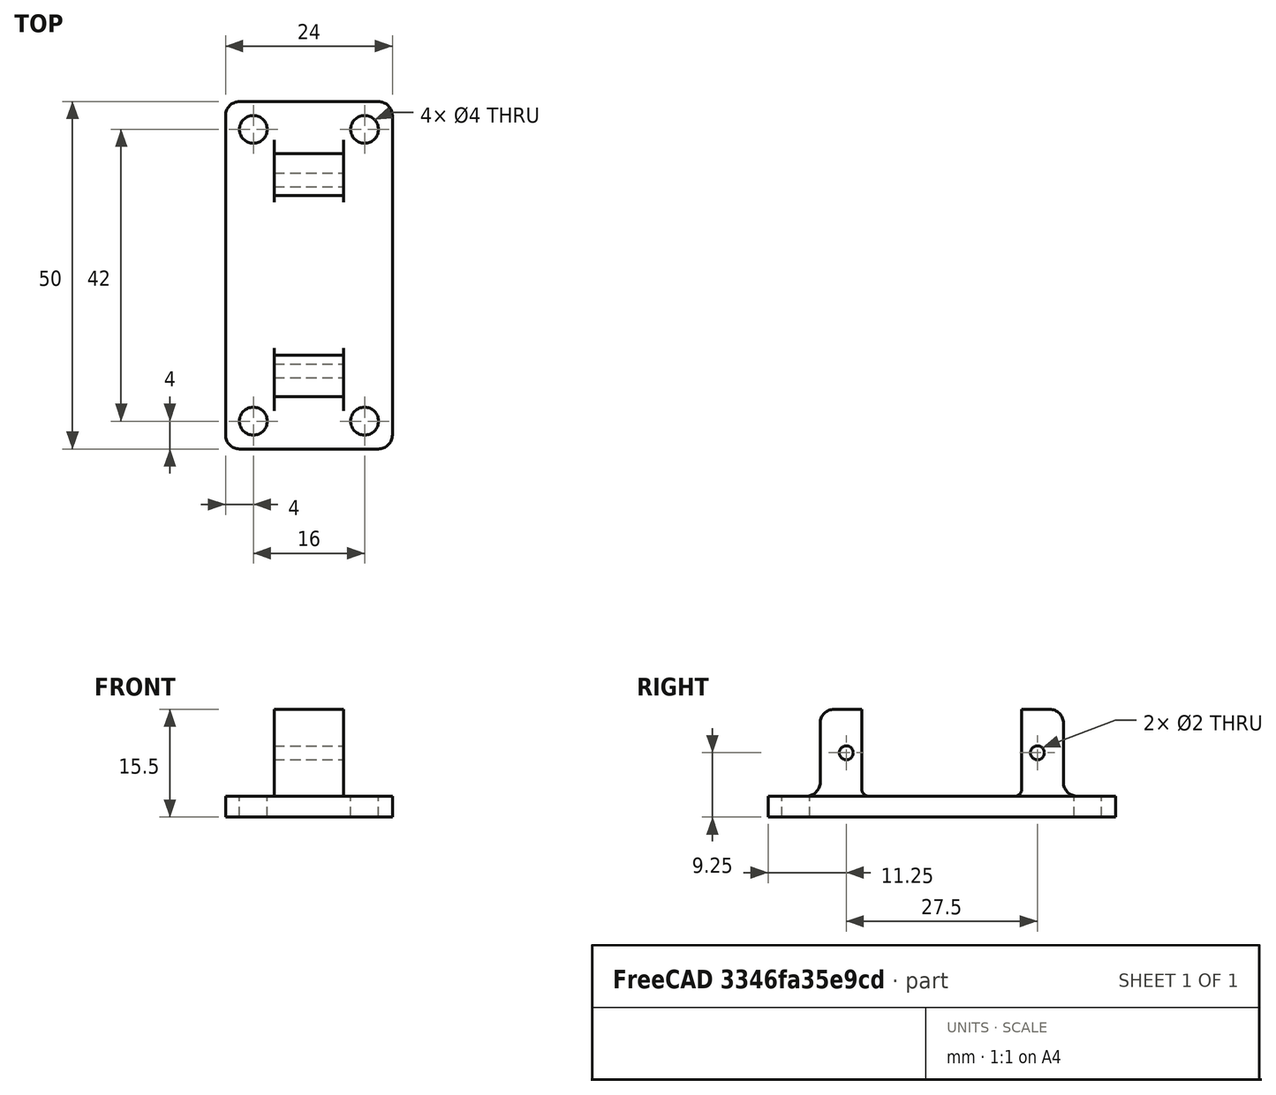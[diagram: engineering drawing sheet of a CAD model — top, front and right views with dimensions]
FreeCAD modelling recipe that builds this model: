
FCSTD DOCUMENT  (FreeCAD 0.19R24276 (Git))
Label: ServoBase
License: All rights reserved
LicenseURL: http://en.wikipedia.org/wiki/All_rights_reserved
objects: Part::Cylinder×6, Part::Fillet×4, Part::Box×3, Part::Cut×2, Part::MultiFuse×2, Spreadsheet::Sheet×1
note: 17 computed .brp shape members not serialized (recipe doc carries the construction recipe); baked Part::Feature solids carry a one-line shape summary decoded from their .brp

FEATURE [Part::Box] Box  label="base"
  AttacherType = Attacher::AttachEngine3D
  Height = 3
  Length = 24
  Width = 50
  expr: Length = <<data>>.base_depth
  expr: Width = <<data>>.base_width
FEATURE [Part::Box] Box001  label="Cube"
  AttacherType = Attacher::AttachEngine3D
  Height = 12.5
  Length = 10
  Placement = pos=(7,7.5,3) rot=(0,0,1;0rad)
  Width = 35
  expr: .Placement.Base.y = (<<data>>.base_width - 35mm) / 2
FEATURE [Part::Box] Box002  label="Cube001"
  AttacherType = Attacher::AttachEngine3D
  Height = 12.5
  Length = 16
  Placement = pos=(7,13.5,3) rot=(0,0,1;0rad)
  Width = 23
  expr: .Placement.Base.y = (<<data>>.base_width - 35mm) / 2 + 6mm
FEATURE [Part::Cut] Cut
  Base = -> Box001
  Tool = -> Box002
FEATURE [Part::Cylinder] Cylinder
  Angle = 360
  AttacherType = Attacher::AttachEngine3D
  Height = 28
  Placement = pos=(0,11.25,9.25) rot=(0,1,0;1.5708rad)
  Radius = 1
  expr: .Placement.Base.y = <<data>>.base_width / 2 - <<data>>.hole_width / 2
FEATURE [Part::Cylinder] Cylinder001
  Angle = 360
  AttacherType = Attacher::AttachEngine3D
  Height = 28
  Placement = pos=(0,38.75,9.25) rot=(0,1,0;1.5708rad)
  Radius = 1
  expr: .Placement.Base.y = <<data>>.base_width / 2 + <<data>>.hole_width / 2
FEATURE [Part::Cylinder] Cylinder002
  Angle = 360
  AttacherType = Attacher::AttachEngine3D
  Height = 10
  Placement = pos=(4,4,0) rot=(0,0,1;0rad)
  Radius = 2
  expr: .Placement.Base.y = 4mm
FEATURE [Part::Cylinder] Cylinder003
  Angle = 360
  AttacherType = Attacher::AttachEngine3D
  Height = 10
  Placement = pos=(4,46,0) rot=(0,0,1;0rad)
  Radius = 2
  expr: .Placement.Base.y = <<data>>.base_width - 4mm
FEATURE [Part::Cylinder] Cylinder004
  Angle = 360
  AttacherType = Attacher::AttachEngine3D
  Height = 10
  Placement = pos=(20,4,0) rot=(0,0,1;0rad)
  Radius = 2
  expr: .Placement.Base.x = <<data>>.base_depth - 4mm
FEATURE [Part::Cylinder] Cylinder005
  Angle = 360
  AttacherType = Attacher::AttachEngine3D
  Height = 10
  Placement = pos=(20,46,0) rot=(0,0,1;0rad)
  Radius = 2
  expr: .Placement.Base.x = <<data>>.base_depth - 4mm
  expr: .Placement.Base.y = <<data>>.base_width - 4mm
FEATURE [Part::Fillet] Fillet
  Base = -> Box
  Edges = 4 edges r=2: [Edge1,Edge3,Edge5,Edge7]
FEATURE [Part::MultiFuse] Fusion001
  Shapes = -> [Cylinder002,Cylinder,Cylinder004,Cylinder005,Cylinder003,Cylinder001]
FEATURE [Spreadsheet::Sheet] Spreadsheet  label="data"
  cells = A2=base_width; B2(base_width)==50mm; A3=hole_width; B3(hole_width)==27.5mm; A4=base_depth; B4(base_depth)==24mm
FEATURE [Part::MultiFuse] Fusion
  Shapes = -> [Fillet,Cut]
FEATURE [Part::Cut] Cut001
  Base = -> Fusion
  Tool = -> Fusion001
FEATURE [Part::Fillet] Fillet001
  Base = -> Cut001
  Edges = 2 edges r=1: [Edge16,Edge19]
FEATURE [Part::Fillet] Fillet002
  Base = -> Fillet001
  Edges = 2 edges r=2: [Edge5,Edge21]
FEATURE [Part::Fillet] Fillet003
  Base = -> Fillet002
  Edges = 2 edges r=2: [Edge81,Edge84]
